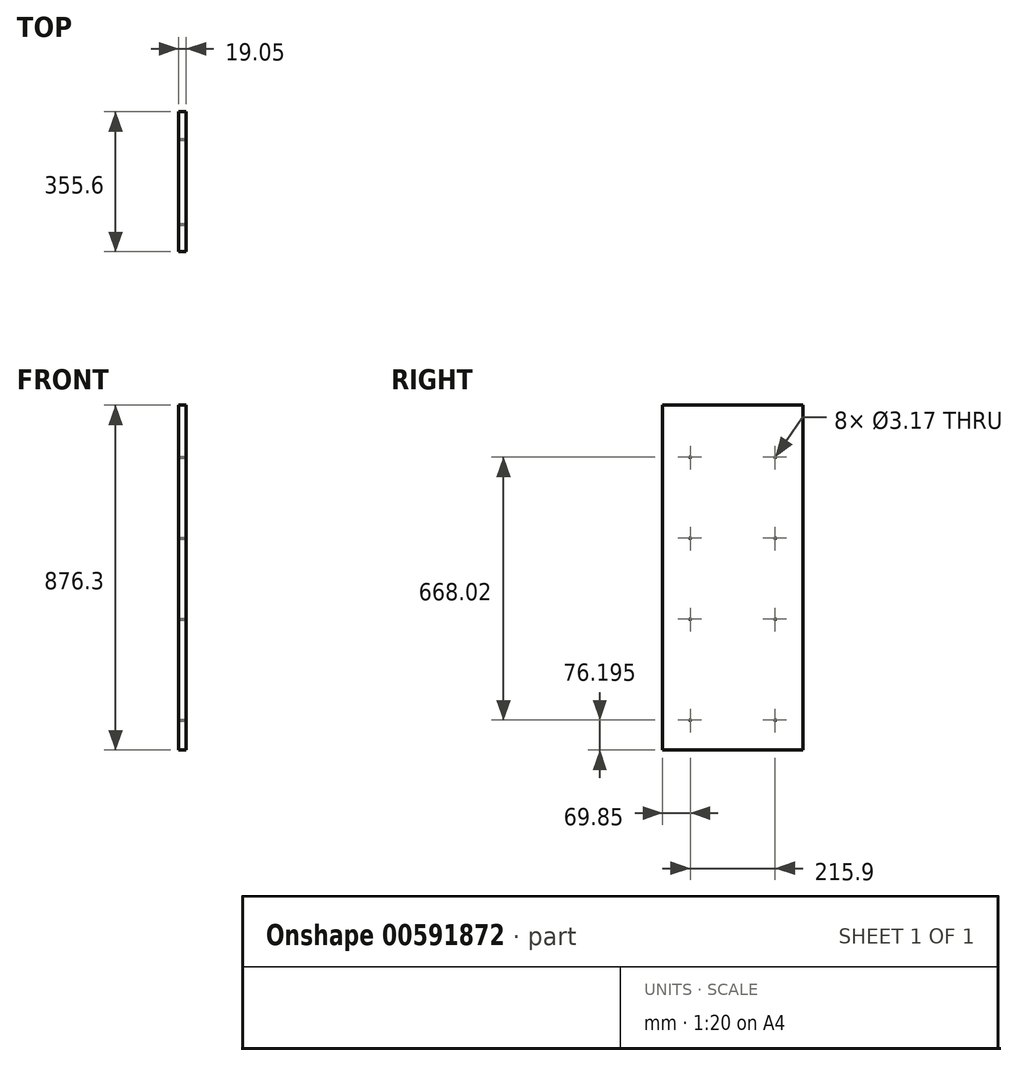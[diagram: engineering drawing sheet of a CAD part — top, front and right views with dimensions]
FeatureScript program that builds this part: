
annotation { "Feature Type Name" : "Feature", "Feature Type Description" : "" }
export const myFeature = defineFeature(function(context is Context, id is Id, definition is map)
    precondition{}
    {
        {
            var Q0;
            Q0=qCreatedBy(makeId("Right.planeOp"),FACE);
            var sketch = newSketch(context, id + "F0", { "sketchPlane" : qUnion([Q0])});
            skLineSegment(sketch, "E0.bottom", {"start": v(177.8, 447.68) * mm, "end": v(-177.8, 447.68) * mm});
            skLineSegment(sketch, "E0.top", {"start": v(177.8, -447.67) * mm, "end": v(-177.8, -447.67) * mm});
            skLineSegment(sketch, "E0.left", {"start": v(177.8, 447.68) * mm, "end": v(177.8, -447.67) * mm});
            skLineSegment(sketch, "E0.right", {"start": v(-177.8, 447.68) * mm, "end": v(-177.8, -447.67) * mm});
            skPoint(sketch, "E0.middle", {"position": v(0, 0) * mm});
            skSolve(sketch);
        }
        {
            var Q0;
            Q0=makeQuery(id+"F0.imprint","IMPRINT",FACE,{"disambiguationData":[TD([[makeQuery(id+"F0.imprint","IMPRINT",EDGE,{"derivedFrom":sQuery(id+"F0.wireOp",EDGE,"E0.bottom")}),1.0]])]});
            extrude(context, id + "F1", {"entities" : qUnion([Q0]), "depth" : 19.05 * mm, "offsetDistance" : 25.4 * mm});
        }
        {
            var Q0;
            Q0=makeQuery(id+"F1.opExtrude","CAP_FACE",FACE,{"disambiguationData":[OSD([sQuery(id+"F0.wireOp",EDGE,"E0.bottom"),sQuery(id+"F0.wireOp",EDGE,"E0.top"),sQuery(id+"F0.wireOp",EDGE,"E0.left"),sQuery(id+"F0.wireOp",EDGE,"E0.right")])],"isStart":false});
            var sketch = newSketch(context, id + "F2", { "sketchPlane" : qUnion([Q0])});
            skLineSegment(sketch, "E1.bottom", {"start": v(-177.8, -447.67) * mm, "end": v(177.8, -447.67) * mm});
            skLineSegment(sketch, "E1.top", {"start": v(-177.8, -428.62) * mm, "end": v(177.8, -428.62) * mm});
            skLineSegment(sketch, "E1.left", {"start": v(-177.8, -447.67) * mm, "end": v(-177.8, -428.62) * mm});
            skLineSegment(sketch, "E1.right", {"start": v(177.8, -447.67) * mm, "end": v(177.8, -428.62) * mm});
            skLineSegment(sketch, "E2", {"start": v(0, -828.68) * mm, "end": v(0, -428.62) * mm});
            skLineSegment(sketch, "E3", {"start": v(-177.8, -352.42) * mm, "end": v(-107.95, -352.42) * mm});
            skLineSegment(sketch, "E4", {"start": v(177.8, -352.42) * mm, "end": v(107.95, -352.42) * mm});
            skLineSegment(sketch, "E5.bottom", {"start": v(-177.8, -428.62) * mm, "end": v(-196.85, -428.62) * mm});
            skLineSegment(sketch, "E5.top", {"start": v(-177.8, -174.62) * mm, "end": v(-196.85, -174.62) * mm});
            skLineSegment(sketch, "E5.left", {"start": v(-177.8, -428.62) * mm, "end": v(-177.8, -174.62) * mm});
            skLineSegment(sketch, "E5.right", {"start": v(-196.85, -428.62) * mm, "end": v(-196.85, -174.62) * mm});
            skLineSegment(sketch, "E6", {"start": v(-196.85, -174.62) * mm, "end": v(-196.85, -172.08) * mm});
            skLineSegment(sketch, "E7.bottom", {"start": v(-196.85, -172.08) * mm, "end": v(-177.8, -172.08) * mm});
            skLineSegment(sketch, "E7.top", {"start": v(-196.85, 31.12) * mm, "end": v(-177.8, 31.12) * mm});
            skLineSegment(sketch, "E7.left", {"start": v(-196.85, -172.08) * mm, "end": v(-196.85, 31.12) * mm});
            skLineSegment(sketch, "E7.right", {"start": v(-177.8, -172.08) * mm, "end": v(-177.8, 31.12) * mm});
            skLineSegment(sketch, "E8", {"start": v(0, -428.62) * mm, "end": v(0, 447.68) * mm});
            skLineSegment(sketch, "E9", {"start": v(-196.85, 31.12) * mm, "end": v(-196.85, 33.66) * mm});
            skLineSegment(sketch, "E10.bottom", {"start": v(-196.85, 33.66) * mm, "end": v(-177.8, 33.66) * mm});
            skLineSegment(sketch, "E10.top", {"start": v(-196.85, 236.86) * mm, "end": v(-177.8, 236.86) * mm});
            skLineSegment(sketch, "E10.left", {"start": v(-196.85, 33.66) * mm, "end": v(-196.85, 236.86) * mm});
            skLineSegment(sketch, "E10.right", {"start": v(-177.8, 33.66) * mm, "end": v(-177.8, 236.86) * mm});
            skLineSegment(sketch, "E11", {"start": v(0, 447.68) * mm, "end": v(-177.8, 447.68) * mm});
            skLineSegment(sketch, "E12", {"start": v(-196.85, 236.86) * mm, "end": v(-196.85, 239.4) * mm});
            skLineSegment(sketch, "E13.bottom", {"start": v(-196.85, 239.4) * mm, "end": v(-177.8, 239.4) * mm});
            skLineSegment(sketch, "E13.top", {"start": v(-196.85, 442.6) * mm, "end": v(-177.8, 442.6) * mm});
            skLineSegment(sketch, "E13.left", {"start": v(-196.85, 239.4) * mm, "end": v(-196.85, 442.6) * mm});
            skLineSegment(sketch, "E13.right", {"start": v(-177.8, 239.4) * mm, "end": v(-177.8, 442.6) * mm});
            skLineSegment(sketch, "E14", {"start": v(-177.8, -172.08) * mm, "end": v(-177.8, -95.88) * mm});
            skLineSegment(sketch, "E15", {"start": v(-177.8, -95.88) * mm, "end": v(-107.95, -95.88) * mm});
            skLineSegment(sketch, "E16", {"start": v(-177.8, 33.66) * mm, "end": v(-177.8, 109.86) * mm});
            skLineSegment(sketch, "E17", {"start": v(-177.8, 109.86) * mm, "end": v(-107.95, 109.86) * mm});
            skLineSegment(sketch, "E18", {"start": v(-177.8, -428.62) * mm, "end": v(-177.8, -352.43) * mm});
            skLineSegment(sketch, "E19", {"start": v(177.8, -428.62) * mm, "end": v(177.8, -352.42) * mm});
            skLineSegment(sketch, "E20", {"start": v(-177.8, 239.4) * mm, "end": v(-177.8, 315.6) * mm});
            skLineSegment(sketch, "E21", {"start": v(-177.8, 315.6) * mm, "end": v(-107.95, 315.6) * mm});
            skLineSegment(sketch, "E22", {"start": v(107.95, -352.42) * mm, "end": v(107.95, -95.88) * mm});
            skLineSegment(sketch, "E23", {"start": v(107.95, -95.88) * mm, "end": v(107.95, 109.86) * mm});
            skLineSegment(sketch, "E24", {"start": v(107.95, 109.86) * mm, "end": v(107.95, 315.6) * mm});
            skPoint(sketch, "E25", {"position": v(-107.95, 315.6) * mm});
            skPoint(sketch, "E26", {"position": v(107.95, 315.6) * mm});
            skPoint(sketch, "E27", {"position": v(107.95, 109.86) * mm});
            skPoint(sketch, "E28", {"position": v(-107.95, 109.86) * mm});
            skPoint(sketch, "E29", {"position": v(-107.95, -95.88) * mm});
            skPoint(sketch, "E30", {"position": v(107.95, -95.88) * mm});
            skPoint(sketch, "E31", {"position": v(-107.95, -352.42) * mm});
            skPoint(sketch, "E32", {"position": v(107.95, -352.42) * mm});
            skSolve(sketch);
        }
        {
            var Q0;
            Q0=sQuery(id+"F2.wireOp",VERTEX,"E25");
            var Q1;
            Q1=sQuery(id+"F2.wireOp",VERTEX,"E26");
            var Q2;
            Q2=sQuery(id+"F2.wireOp",VERTEX,"E27");
            var Q3;
            Q3=sQuery(id+"F2.wireOp",VERTEX,"E28");
            var Q4;
            Q4=sQuery(id+"F2.wireOp",VERTEX,"E29");
            var Q5;
            Q5=sQuery(id+"F2.wireOp",VERTEX,"E30");
            var Q6;
            Q6=sQuery(id+"F2.wireOp",VERTEX,"E32");
            var Q7;
            Q7=sQuery(id+"F2.wireOp",VERTEX,"E31");
            var Q8;
            Q8=makeQuery(id+"F1.opExtrude","SWEPT_BODY",BODY,{"disambiguationData":[OSD([sQuery(id+"F0.wireOp",EDGE,"E0.bottom"),sQuery(id+"F0.wireOp",EDGE,"E0.top"),sQuery(id+"F0.wireOp",EDGE,"E0.left"),sQuery(id+"F0.wireOp",EDGE,"E0.right")])]});
            hole(context, id + "F3", {"style" : HoleStyle.SIMPLE, "endStyle" : HoleEndStyle.BLIND, "holeDiameter" : 3.17 * mm, "majorDiameter" : 6.35 * mm, "holeDepth" : 19.05 * mm, "isTappedThrough" : true, "tappedDepth" : 12.7 * mm, "tapClearance" : 3, "startFromSketch" : true, "locations" : qUnion([Q0, Q1, Q2, Q3, Q4, Q5, Q6, Q7]), "scope" : qUnion([Q8])});
        }
        {
            var Q0;
            Q0=makeQuery(id+"F1.opExtrude","SWEPT_FACE",FACE,{"disambiguationData":[OSD([sQuery(id+"F0.wireOp",EDGE,"E0.top")])]});
            extrude(context, id + "F4", {"entities" : qUnion([Q0]), "operationType" : NewBodyOperationType.REMOVE, "oppositeDirection" : true, "depth" : 19.05 * mm, "offsetDistance" : 25.4 * mm});
        }
    });
